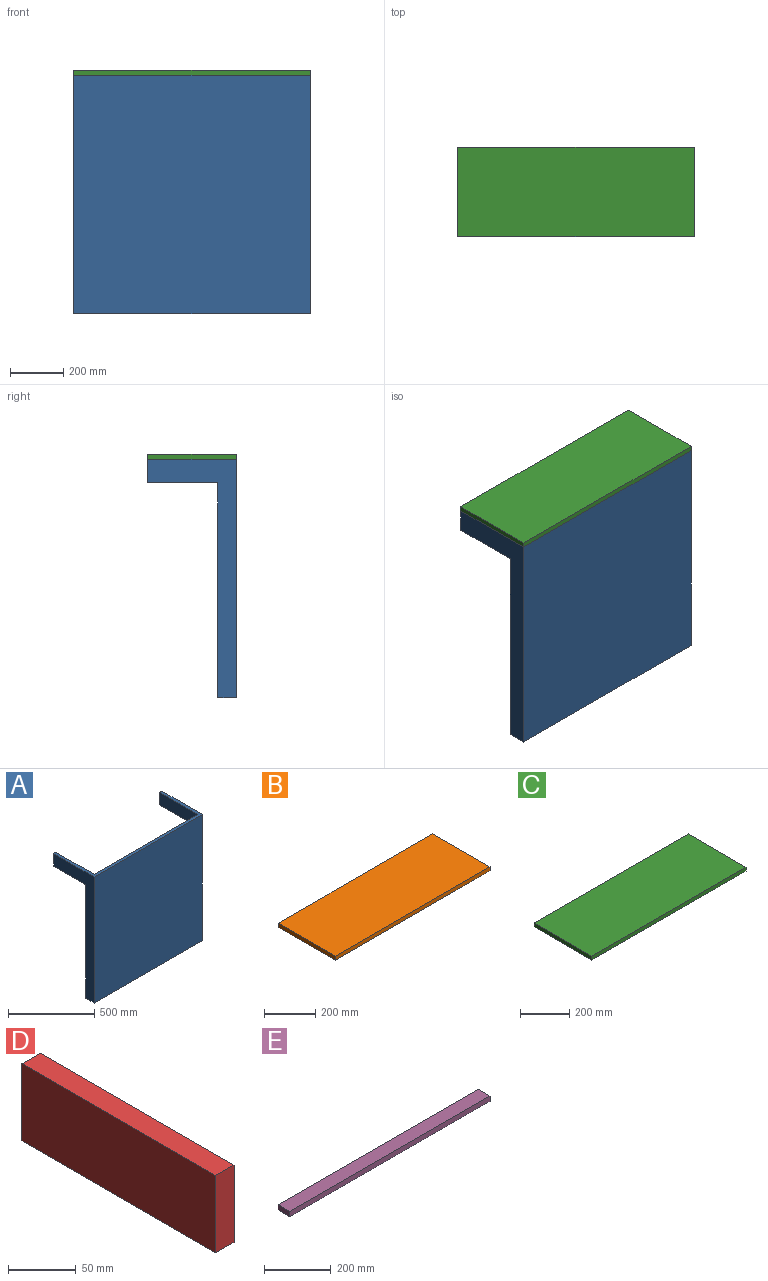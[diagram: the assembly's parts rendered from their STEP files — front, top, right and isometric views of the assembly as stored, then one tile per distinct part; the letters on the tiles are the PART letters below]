
ASSEMBLY  parts=5 mates=4
PART A: 14 faces, bbox 889x333.4x895.4 mm
  f0: plane 895.35x850.9mm, normal (0,1,0), area 761853.3mm2, adj f2,f4,f6,f8
  f1: plane 895.35x333.38mm, normal (-1,0,0), area 85967.6mm2, adj f2,f4,f5,f9,f12,f13
  f2: plane 889x69.85mm, normal (0,0,-1), area 18870.9mm2, adj f0,f1,f3,f5,f6,f7,f8,f9
  f3: plane 895.35x333.38mm, normal (1,0,0), area 85967.6mm2, adj f2,f4,f5,f7,f10,f11
  f4: plane 889x333.38mm, normal (0,0,1), area 28911.2mm2, adj f0,f1,f3,f5,f6,f8,f11,f13
  f5: plane 895.35x889mm, normal (0,-1,0), area 795966.2mm2, adj f1,f2,f3,f4
  f6: plane 895.35x314.33mm, normal (-1,0,0), area 68911.2mm2, adj f0,f2,f4,f7,f10,f11
  f7: plane 806.45x19.05mm, normal (0,1,0), area 15362.9mm2, adj f2,f3,f6,f10
  f8: plane 895.35x314.33mm, normal (1,0,0), area 68911.2mm2, adj f0,f2,f4,f9,f12,f13
  f9: plane 806.45x19.05mm, normal (0,1,0), area 15362.9mm2, adj f1,f2,f8,f12
  f10: plane 263.53x19.05mm, normal (0,0,-1), area 5020.2mm2, adj f3,f6,f7,f11
  f11: plane 88.9x19.05mm, normal (0,1,0), area 1693.5mm2, adj f3,f4,f6,f10
  f12: plane 263.53x19.05mm, normal (0,0,-1), area 5020.2mm2, adj f1,f8,f9,f13
  f13: plane 88.9x19.05mm, normal (0,1,0), area 1693.5mm2, adj f1,f4,f8,f12
PART B: 6 faces, bbox 850.9x314.3x19.1 mm
  f0: plane 850.9x19.05mm, normal (0,-1,0), area 16209.6mm2, adj f1,f3,f4,f5
  f1: plane 314.33x19.05mm, normal (1,0,0), area 5987.9mm2, adj f0,f2,f4,f5
  f2: plane 850.9x19.05mm, normal (0,1,0), area 16209.6mm2, adj f1,f3,f4,f5
  f3: plane 314.33x19.05mm, normal (-1,0,0), area 5987.9mm2, adj f0,f2,f4,f5
  f4: plane 850.9x314.33mm, normal (0,0,1), area 267459.1mm2, adj f0,f1,f2,f3
  f5: plane 850.9x314.33mm, normal (0,0,-1), area 267459.1mm2, adj f0,f1,f2,f3
PART C: 6 faces, bbox 889x333.4x19.1 mm
  f0: plane 333.38x19.05mm, normal (-1,0,0), area 6350.8mm2, adj f1,f3,f4,f5
  f1: plane 889x19.05mm, normal (0,-1,0), area 16935.5mm2, adj f0,f2,f4,f5
  f2: plane 333.38x19.05mm, normal (1,0,0), area 6350.8mm2, adj f1,f3,f4,f5
  f3: plane 889x19.05mm, normal (0,1,0), area 16935.5mm2, adj f0,f2,f4,f5
  f4: plane 889x333.38mm, normal (0,0,1), area 296370.4mm2, adj f0,f1,f2,f3
  f5: plane 889x333.38mm, normal (0,0,-1), area 296370.4mm2, adj f0,f1,f2,f3
PART D: 6 faces, bbox 19.1x202.4x69.9 mm
  f0: plane 202.36x19.05mm, normal (0,0,-1), area 3854.9mm2, adj f1,f3,f4,f5
  f1: plane 69.85x19.05mm, normal (0,1,0), area 1330.6mm2, adj f0,f2,f4,f5
  f2: plane 202.36x19.05mm, normal (0,0,1), area 3854.9mm2, adj f1,f3,f4,f5
  f3: plane 69.85x19.05mm, normal (0,-1,0), area 1330.6mm2, adj f0,f2,f4,f5
  f4: plane 202.36x69.85mm, normal (1,0,0), area 14134.5mm2, adj f0,f1,f2,f3
  f5: plane 202.36x69.85mm, normal (-1,0,0), area 14134.5mm2, adj f0,f1,f2,f3
PART E: 6 faces, bbox 850.9x50.8x19.1 mm
  f0: plane 50.8x19.05mm, normal (-1,0,0), area 967.7mm2, adj f1,f3,f4,f5
  f1: plane 850.9x19.05mm, normal (0,-1,0), area 16209.6mm2, adj f0,f2,f4,f5
  f2: plane 50.8x19.05mm, normal (1,0,0), area 967.7mm2, adj f1,f3,f4,f5
  f3: plane 850.9x19.05mm, normal (0,1,0), area 16209.6mm2, adj f0,f2,f4,f5
  f4: plane 850.9x50.8mm, normal (0,0,1), area 43225.7mm2, adj f0,f1,f2,f3
  f5: plane 850.9x50.8mm, normal (0,0,-1), area 43225.7mm2, adj f0,f1,f2,f3
PLACE A t=(883.81,182.98,-269.48)mm
PLACE B t=(883.81,340.14,89.3)mm
PLACE C t=(883.81,330.62,178.2)mm
PLACE D t=(874.29,396.13,143.27)mm
PLACE E t=(883.81,208.38,-717.15)mm
MATE planar B.f1 <-> A.f6  axis (1,0,0) through (1309.26,497.3,89.3)mm
MATE planar E.f0 <-> A.f8  axis (-1,0,0) through (458.36,233.78,-717.15)mm
MATE planar C.f5 <-> A.f4  axis (0,0,-1) through (1328.31,163.93,178.2)mm
MATE planar D.f2 <-> C.f5  axis (0,0,1) through (883.81,497.3,178.2)mm
